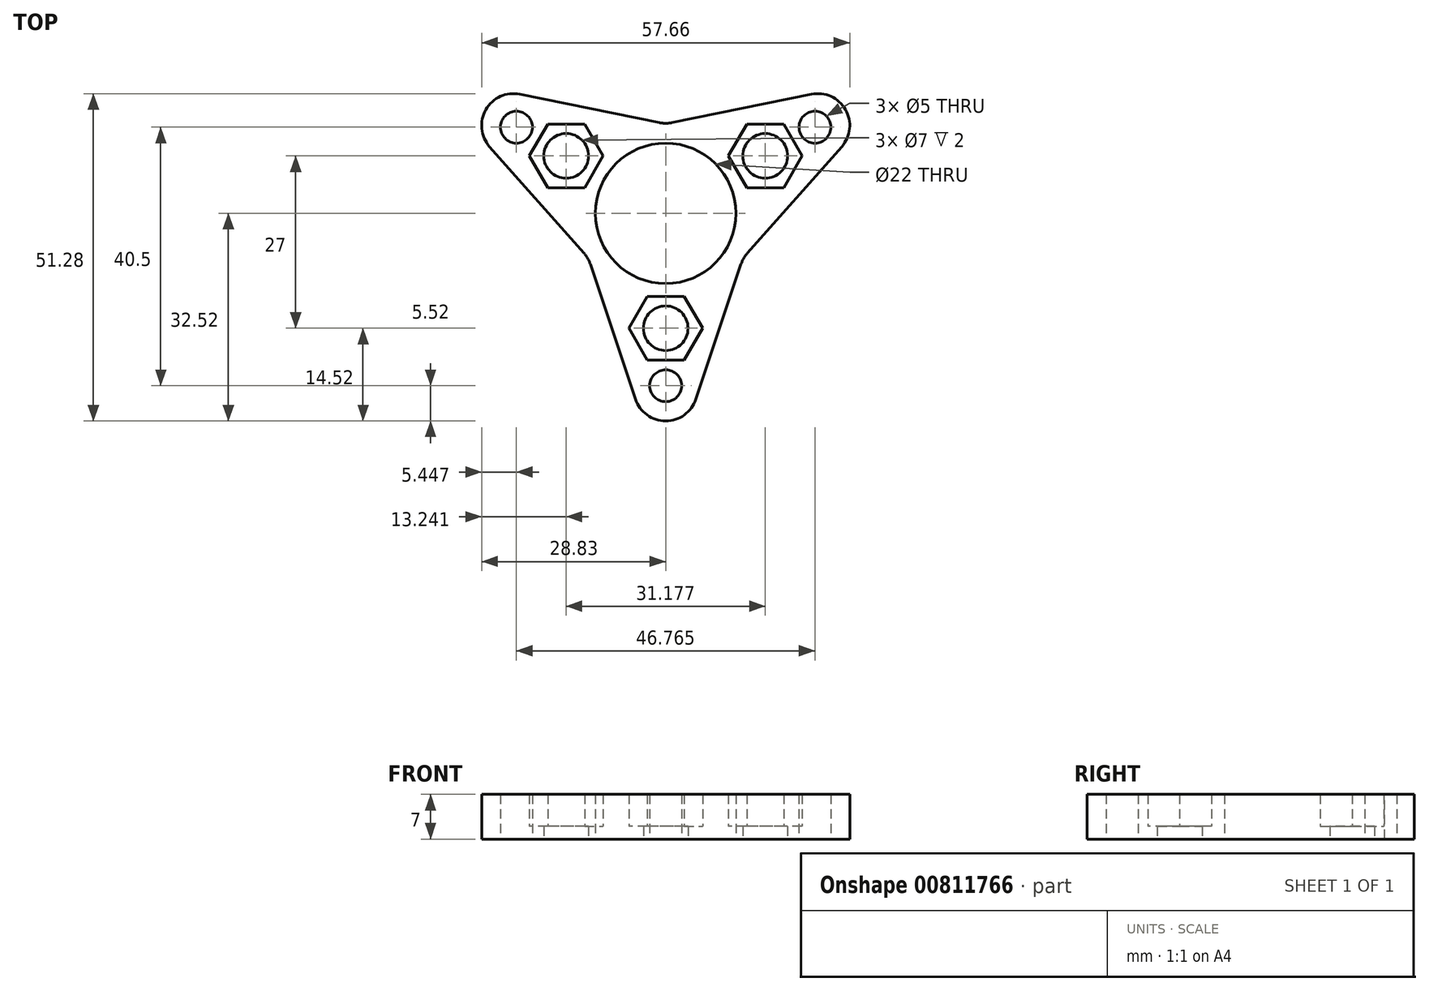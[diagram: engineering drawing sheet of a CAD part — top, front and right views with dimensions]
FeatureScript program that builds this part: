
annotation { "Feature Type Name" : "Feature", "Feature Type Description" : "" }
export const myFeature = defineFeature(function(context is Context, id is Id, definition is map)
    precondition{}
    {
        {
            var Q0;
            Q0=qCreatedBy(makeId("Top.planeOp"),FACE);
            var sketch = newSketch(context, id + "F0", { "sketchPlane" : qUnion([Q0])});
            skCircle(sketch, "E0", {"center": v(0, 0) * mm, "radius": 11 * mm});
            skCircle(sketch, "E1.cCircle", {"center": v(-15.59, 9) * mm, "radius": 5 * mm, "construction": true});
            skLineSegment(sketch, "E1.0", {"start": v(-18.48, 4) * mm, "end": v(-21.36, 9) * mm});
            skLineSegment(sketch, "E1.1", {"start": v(-21.36, 9) * mm, "end": v(-18.48, 14) * mm});
            skLineSegment(sketch, "E1.2", {"start": v(-18.48, 14) * mm, "end": v(-12.7, 14) * mm});
            skLineSegment(sketch, "E1.3", {"start": v(-12.7, 14) * mm, "end": v(-9.81, 9) * mm});
            skLineSegment(sketch, "E1.4", {"start": v(-9.81, 9) * mm, "end": v(-12.7, 4) * mm});
            skLineSegment(sketch, "E1.5", {"start": v(-12.7, 4) * mm, "end": v(-18.48, 4) * mm});
            skPoint(sketch, "E1.0.midPoint", {"position": v(-19.92, 6.5) * mm});
            skCircle(sketch, "E2.cCircle", {"center": v(15.59, 9) * mm, "radius": 5 * mm, "construction": true});
            skLineSegment(sketch, "E2.0", {"start": v(18.48, 4) * mm, "end": v(12.7, 4) * mm});
            skLineSegment(sketch, "E2.1", {"start": v(12.7, 4) * mm, "end": v(9.81, 9) * mm});
            skLineSegment(sketch, "E2.2", {"start": v(9.81, 9) * mm, "end": v(12.7, 14) * mm});
            skLineSegment(sketch, "E2.3", {"start": v(12.7, 14) * mm, "end": v(18.48, 14) * mm});
            skLineSegment(sketch, "E2.4", {"start": v(18.48, 14) * mm, "end": v(21.36, 9) * mm});
            skLineSegment(sketch, "E2.5", {"start": v(21.36, 9) * mm, "end": v(18.48, 4) * mm});
            skPoint(sketch, "E2.0.midPoint", {"position": v(15.59, 4) * mm});
            skLineSegment(sketch, "E3", {"start": v(0, 0) * mm, "end": v(-37.5, 21.65) * mm, "construction": true});
            skLineSegment(sketch, "E4", {"start": v(0, 0) * mm, "end": v(37.5, 21.65) * mm, "construction": true});
            skCircle(sketch, "E5.cCircle", {"center": v(0, -18) * mm, "radius": 5 * mm, "construction": true});
            skLineSegment(sketch, "E5.0", {"start": v(5.77, -18) * mm, "end": v(2.89, -23) * mm});
            skLineSegment(sketch, "E5.1", {"start": v(2.89, -23) * mm, "end": v(-2.89, -23) * mm});
            skLineSegment(sketch, "E5.2", {"start": v(-2.89, -23) * mm, "end": v(-5.77, -18) * mm});
            skLineSegment(sketch, "E5.3", {"start": v(-5.77, -18) * mm, "end": v(-2.89, -13) * mm});
            skLineSegment(sketch, "E5.4", {"start": v(-2.89, -13) * mm, "end": v(2.89, -13) * mm});
            skLineSegment(sketch, "E5.5", {"start": v(2.89, -13) * mm, "end": v(5.77, -18) * mm});
            skPoint(sketch, "E5.0.midPoint", {"position": v(4.33, -20.5) * mm});
            skLineSegment(sketch, "E6", {"start": v(0, 0) * mm, "end": v(23.11, -13.34) * mm, "construction": true});
            skLineSegment(sketch, "E7", {"start": v(0, 0) * mm, "end": v(-25.4, -14.67) * mm, "construction": true});
            skPoint(sketch, "E8.0.midPoint", {"position": v(18.75, -10.83) * mm});
            skCircle(sketch, "E9", {"center": v(-15.59, 9) * mm, "radius": 3.5 * mm});
            skCircle(sketch, "E10", {"center": v(15.59, 9) * mm, "radius": 3.5 * mm});
            skCircle(sketch, "E11", {"center": v(0, -18) * mm, "radius": 3.5 * mm});
            skLineSegment(sketch, "E12", {"start": v(0, 0) * mm, "end": v(0, -52.9) * mm, "construction": true});
            skLineSegment(sketch, "E13", {"start": v(-37.5, 21.65) * mm, "end": v(-12.12, -7) * mm});
            skLineSegment(sketch, "E14", {"start": v(-12.12, -7) * mm, "end": v(0, -43.3) * mm});
            skLineSegment(sketch, "E15", {"start": v(0, -43.3) * mm, "end": v(12.12, -7) * mm});
            skLineSegment(sketch, "E16", {"start": v(12.12, -7) * mm, "end": v(37.5, 21.65) * mm});
            skLineSegment(sketch, "E17", {"start": v(0, 0) * mm, "end": v(0, 47.54) * mm, "construction": true});
            skLineSegment(sketch, "E18", {"start": v(-37.5, 21.65) * mm, "end": v(0, 14) * mm});
            skLineSegment(sketch, "E19", {"start": v(0, 14) * mm, "end": v(37.5, 21.65) * mm});
            skCircle(sketch, "E20", {"center": v(0, -27) * mm, "radius": 2.5 * mm});
            skCircle(sketch, "E21", {"center": v(23.38, 13.5) * mm, "radius": 2.5 * mm});
            skCircle(sketch, "E22", {"center": v(-23.38, 13.5) * mm, "radius": 2.5 * mm});
            skSolve(sketch);
        }
        {
            var Q0;
            Q0=makeQuery(id+"F0.imprint","IMPRINT",FACE,{"disambiguationData":[TD([[makeQuery(id+"F0.imprint","IMPRINT",EDGE,{"derivedFrom":sQuery(id+"F0.wireOp",EDGE,"E0")}),-1.0]])]});
            extrude(context, id + "F1", {"entities" : qUnion([Q0]), "depth" : 7 * mm, "offsetDistance" : 25 * mm});
        }
        {
            var Q0;
            Q0=makeQuery(id+"F0.imprint","IMPRINT",FACE,{"disambiguationData":[TD([[makeQuery(id+"F0.imprint","IMPRINT",EDGE,{"derivedFrom":sQuery(id+"F0.wireOp",EDGE,"ee9d131a-520a-490e-a8ce-2a2484e60bbd.0")}),-1.0]])]});
            var Q1;
            Q1=makeQuery(id+"F0.imprint","IMPRINT",FACE,{"disambiguationData":[TD([[makeQuery(id+"F0.imprint","IMPRINT",EDGE,{"derivedFrom":sQuery(id+"F0.wireOp",EDGE,"E1.0")}),-1.0]])]});
            var Q2;
            Q2=makeQuery(id+"F0.imprint","IMPRINT",FACE,{"disambiguationData":[TD([[makeQuery(id+"F0.imprint","IMPRINT",EDGE,{"derivedFrom":sQuery(id+"F0.wireOp",EDGE,"82c2bf3c-1cb3-4f29-a97b-33669777ac8e.0")}),-1.0]])]});
            var Q3;
            Q3=makeQuery(id+"F0.imprint","IMPRINT",FACE,{"disambiguationData":[TD([[makeQuery(id+"F0.imprint","IMPRINT",EDGE,{"derivedFrom":sQuery(id+"F0.wireOp",EDGE,"567834c8-5c87-4ac2-9c70-8a587ee8b31d.0")}),-1.0]])]});
            var Q4;
            Q4=makeQuery(id+"F0.imprint","IMPRINT",FACE,{"disambiguationData":[TD([[makeQuery(id+"F0.imprint","IMPRINT",EDGE,{"derivedFrom":sQuery(id+"F0.wireOp",EDGE,"E5.0")}),-1.0]])]});
            var Q5;
            Q5=makeQuery(id+"F0.imprint","IMPRINT",FACE,{"disambiguationData":[TD([[makeQuery(id+"F0.imprint","IMPRINT",EDGE,{"derivedFrom":sQuery(id+"F0.wireOp",EDGE,"86d28253-4066-4c5c-9b93-3dc30c01c6ca.0")}),-1.0]])]});
            var Q6;
            Q6=makeQuery(id+"F0.imprint","IMPRINT",FACE,{"disambiguationData":[TD([[makeQuery(id+"F0.imprint","IMPRINT",EDGE,{"derivedFrom":sQuery(id+"F0.wireOp",EDGE,"a4c07e76-bf4a-4a18-a39f-29183dc948d3.0")}),-1.0]])]});
            var Q7;
            Q7=makeQuery(id+"F0.imprint","IMPRINT",FACE,{"disambiguationData":[TD([[makeQuery(id+"F0.imprint","IMPRINT",EDGE,{"derivedFrom":sQuery(id+"F0.wireOp",EDGE,"E2.0")}),-1.0]])]});
            var Q8;
            Q8=makeQuery(id+"F0.imprint","IMPRINT",FACE,{"disambiguationData":[TD([[makeQuery(id+"F0.imprint","IMPRINT",EDGE,{"derivedFrom":sQuery(id+"F0.wireOp",EDGE,"f395e505-8d75-4033-b9a1-cf839518a5ec.0")}),-1.0]])]});
            extrude(context, id + "F2", {"entities" : qUnion([Q0, Q1, Q2, Q3, Q4, Q5, Q6, Q7, Q8]), "operationType" : NewBodyOperationType.ADD, "depth" : 2 * mm, "offsetDistance" : 25 * mm});
        }
        {
            var Q0;
            Q0=makeQuery(id+"F1.opExtrude","SWEPT_EDGE",EDGE,{"disambiguationData":[OSD([sQuery(id+"F0.wireOp",EDGE,"E16"),sQuery(id+"F0.wireOp",EDGE,"E19")])]});
            var Q1;
            Q1=makeQuery(id+"F1.opExtrude","SWEPT_EDGE",EDGE,{"disambiguationData":[OSD([sQuery(id+"F0.wireOp",EDGE,"E13"),sQuery(id+"F0.wireOp",EDGE,"E18")])]});
            var Q2;
            Q2=makeQuery(id+"F1.opExtrude","SWEPT_EDGE",EDGE,{"disambiguationData":[OSD([sQuery(id+"F0.wireOp",EDGE,"E14"),sQuery(id+"F0.wireOp",EDGE,"E15")])]});
            var Q3;
            Q3=makeQuery(id+"F1.opExtrude","SWEPT_EDGE",EDGE,{"disambiguationData":[OSD([sQuery(id+"F0.wireOp",EDGE,"E13"),sQuery(id+"F0.wireOp",EDGE,"E14")])]});
            var Q4;
            Q4=makeQuery(id+"F1.opExtrude","SWEPT_EDGE",EDGE,{"disambiguationData":[OSD([sQuery(id+"F0.wireOp",EDGE,"E18"),sQuery(id+"F0.wireOp",EDGE,"E19")])]});
            var Q5;
            Q5=makeQuery(id+"F1.opExtrude","SWEPT_EDGE",EDGE,{"disambiguationData":[OSD([sQuery(id+"F0.wireOp",EDGE,"E15"),sQuery(id+"F0.wireOp",EDGE,"E16")])]});
            fillet(context, id + "F3", {"entities" : qUnion([Q0, Q1, Q2, Q3, Q4, Q5]), "radius" : 5 * mm, "tangentPropagation" : true, "allowEdgeOverflow" : false});
        }
    });
